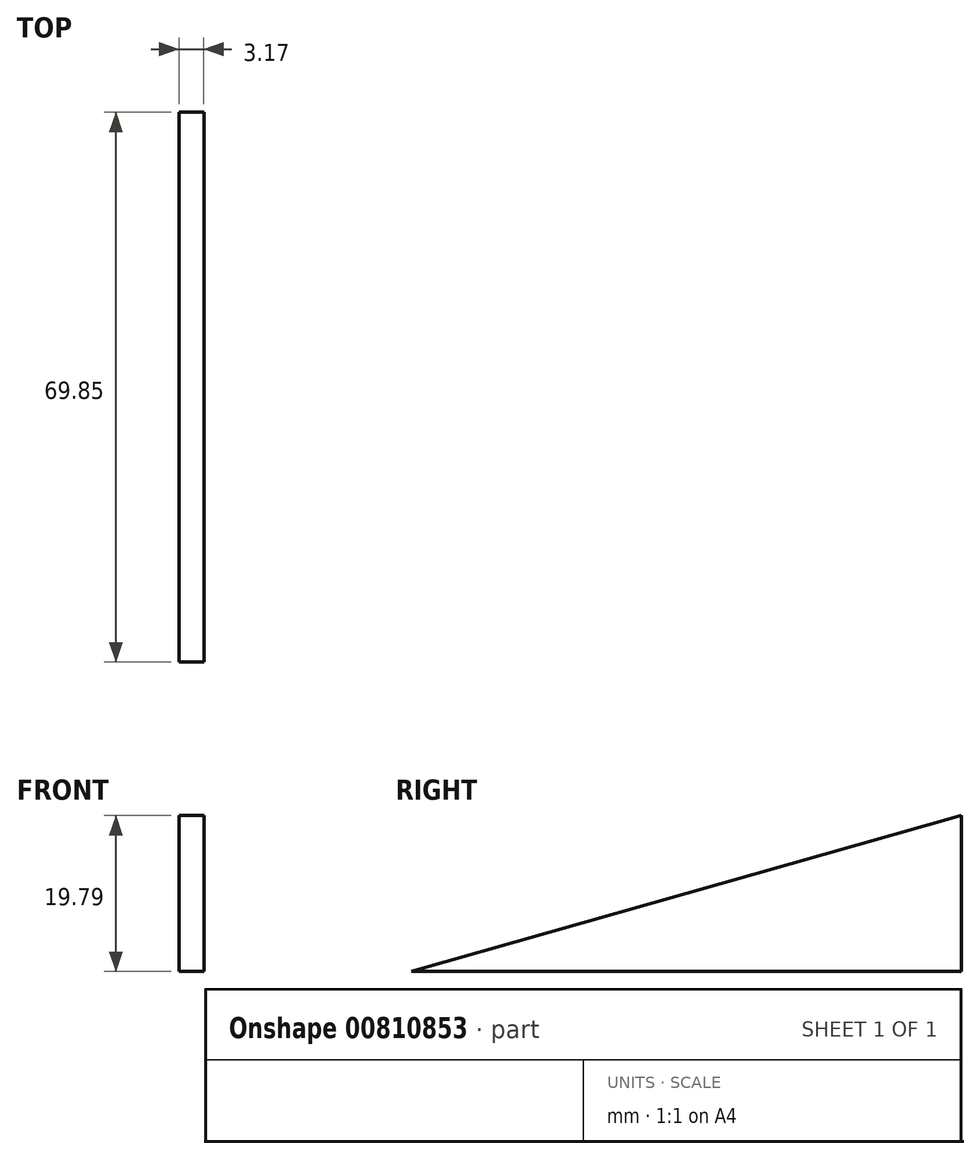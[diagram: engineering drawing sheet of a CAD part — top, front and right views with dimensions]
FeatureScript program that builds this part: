
annotation { "Feature Type Name" : "Feature", "Feature Type Description" : "" }
export const myFeature = defineFeature(function(context is Context, id is Id, definition is map)
    precondition{}
    {
        {
            var Q0;
            Q0=qCreatedBy(makeId("Right.planeOp"),FACE);
            var sketch = newSketch(context, id + "F0", { "sketchPlane" : qUnion([Q0])});
            skLineSegment(sketch, "E0", {"start": v(56.71, -19.8) * mm, "end": v(-13.14, -19.8) * mm});
            skLineSegment(sketch, "E1", {"start": v(-13.14, -19.8) * mm, "end": v(56.71, 0) * mm});
            skLineSegment(sketch, "E2", {"start": v(56.71, 0) * mm, "end": v(56.71, -19.8) * mm});
            skSolve(sketch);
        }
        {
            var Q0;
            Q0=makeQuery(id+"F0.imprint","IMPRINT",FACE,{"disambiguationData":[TD([[makeQuery(id+"F0.imprint","IMPRINT",EDGE,{"derivedFrom":sQuery(id+"F0.wireOp",EDGE,"E0")}),-1.0]])]});
            extrude(context, id + "F1", {"entities" : qUnion([Q0]), "depth" : 3.17 * mm, "offsetDistance" : 25.4 * mm});
        }
    });
